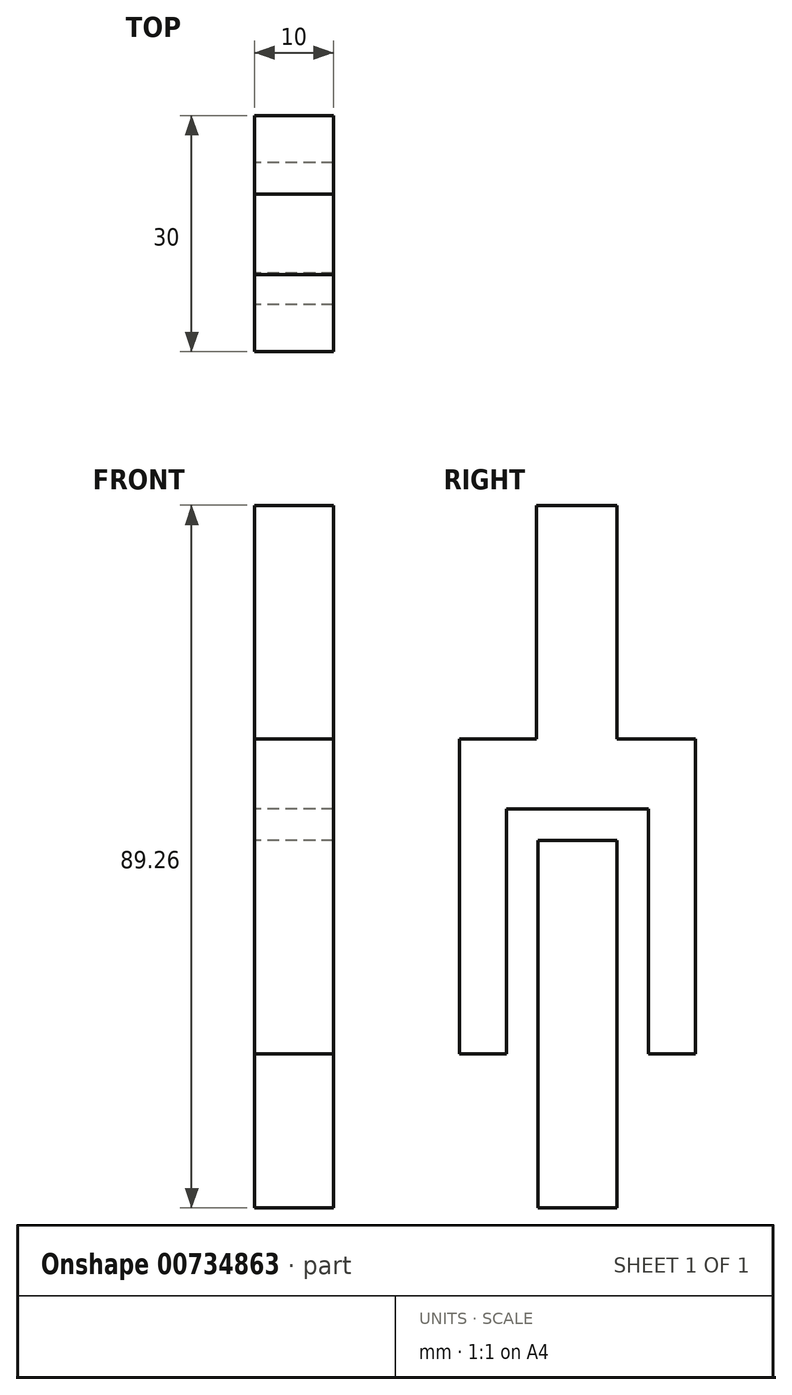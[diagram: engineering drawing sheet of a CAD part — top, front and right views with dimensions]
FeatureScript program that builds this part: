
annotation { "Feature Type Name" : "Feature", "Feature Type Description" : "" }
export const myFeature = defineFeature(function(context is Context, id is Id, definition is map)
    precondition{}
    {
        {
            var Q0;
            Q0=qCreatedBy(makeId("Right.planeOp"),FACE);
            var sketch = newSketch(context, id + "F0", { "sketchPlane" : qUnion([Q0])});
            skLineSegment(sketch, "E0.bottom", {"start": v(0, 0) * mm, "end": v(6, 0) * mm});
            skLineSegment(sketch, "E0.top", {"start": v(0, 40) * mm, "end": v(9.78, 40) * mm});
            skLineSegment(sketch, "E0.left", {"start": v(0, 0) * mm, "end": v(0, 40) * mm});
            skLineSegment(sketch, "E0.right", {"start": v(30, 0) * mm, "end": v(30, 40) * mm});
            skLineSegment(sketch, "E1", {"start": v(15, 27.08) * mm, "end": v(20, 27.08) * mm});
            skLineSegment(sketch, "E2", {"start": v(15, 27.08) * mm, "end": v(10, 27.08) * mm});
            skLineSegment(sketch, "E3", {"start": v(10, 27.08) * mm, "end": v(10, 0) * mm});
            skLineSegment(sketch, "E4", {"start": v(20, 0) * mm, "end": v(20, 27.08) * mm});
            skLineSegment(sketch, "E5", {"start": v(10, 0) * mm, "end": v(10, -19.6) * mm});
            skLineSegment(sketch, "E6", {"start": v(10, -19.6) * mm, "end": v(20, -19.6) * mm});
            skLineSegment(sketch, "E7", {"start": v(20, -19.6) * mm, "end": v(20, 0) * mm});
            skLineSegment(sketch, "E8.0", {"start": v(6, 27.08) * mm, "end": v(6, 0) * mm});
            skLineSegment(sketch, "E9.0", {"start": v(24, 0) * mm, "end": v(24, 27.08) * mm});
            skLineSegment(sketch, "E10.0", {"start": v(15, 31.08) * mm, "end": v(10, 31.08) * mm});
            skLineSegment(sketch, "E11.0", {"start": v(15, 31.08) * mm, "end": v(20, 31.08) * mm});
            skLineSegment(sketch, "E12", {"start": v(10, 31.08) * mm, "end": v(6, 31.08) * mm});
            skLineSegment(sketch, "E13", {"start": v(6, 31.08) * mm, "end": v(6, 27.08) * mm});
            skLineSegment(sketch, "E14", {"start": v(24, 27.08) * mm, "end": v(24, 31.08) * mm});
            skLineSegment(sketch, "E15", {"start": v(24, 31.08) * mm, "end": v(20, 31.08) * mm});
            skLineSegment(sketch, "E16.trimOffspring", {"start": v(24, 0) * mm, "end": v(30, 0) * mm});
            skLineSegment(sketch, "E17", {"start": v(15, 69.67) * mm, "end": v(20, 69.67) * mm});
            skLineSegment(sketch, "E18", {"start": v(20, 69.67) * mm, "end": v(20, 40) * mm});
            skLineSegment(sketch, "E19", {"start": v(15, 69.67) * mm, "end": v(9.78, 69.67) * mm});
            skLineSegment(sketch, "E20", {"start": v(9.78, 69.67) * mm, "end": v(9.78, 40) * mm});
            skLineSegment(sketch, "E21.trimOffspring", {"start": v(20, 40) * mm, "end": v(30, 40) * mm});
            skSolve(sketch);
        }
        {
            var Q0;
            Q0=makeQuery(id+"F0.imprint","IMPRINT",FACE,{"disambiguationData":[TD([[makeQuery(id+"F0.imprint","IMPRINT",EDGE,{"derivedFrom":sQuery(id+"F0.wireOp",EDGE,"E0.bottom")}),1.0]])]});
            var Q1;
            Q1=makeQuery(id+"F0.imprint","IMPRINT",FACE,{"disambiguationData":[TD([[makeQuery(id+"F0.imprint","IMPRINT",EDGE,{"derivedFrom":sQuery(id+"F0.wireOp",EDGE,"E1")}),-1.0]])]});
            extrude(context, id + "F1", {"entities" : qUnion([Q0, Q1]), "depth" : 10 * mm, "offsetDistance" : 25 * mm});
        }
    });
